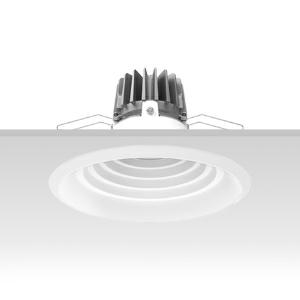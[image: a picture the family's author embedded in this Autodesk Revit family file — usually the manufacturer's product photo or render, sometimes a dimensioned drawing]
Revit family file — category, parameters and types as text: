
# Revit family: 3f_filippi_-_3f_reno_bianco_ugr_3f_filippi_-_30737_-_3f_reno_200_wh_2000-840_ep_ugr
name_source: partatom
category: Lighting Fixtures
units: mm (PartAtom-declared; Revit-internal decimal feet)

## family parameters
Cut with Voids When Loaded = No
Host = Face
Light Source = No
Part Type = Normal
Room Calculation Point = No
Round Connector Dimension = Use Diameter
Shared = No

## types (1)
- 3F Filippi - 3F Reno Bianco UGR (1 x LED, 2458 lm, 21 W, 4000 K)
    Apparent Load = 21 VA
    Approval mark = ENEC
    CIE Flux Codes = 90 100 100 100 100
    Color Rendering = 80
    Color Temperature = 4000 K
    Control Gear = Electronic ballast
    Default Elevation = 1800 mm
    Description = ILLUMINOTECHNICAL
Luminous efficiency 100% (DLOR 100%, ULOR 0%).
Initial luminous flux of the luminaire 2458 lm.
Emergency luminaire luminous flux BLF 20%.
Direct symmetric UGR distribution.
Installation Interdistance Transv.D = 0.99 x hu - Long.D = 1.01 x hu.
Average luminance <500 cd/m² for radial angles >65°.
Tabular UGR (CIE 117 - 4H-8H; S=0.25H; 70/50/20): RUG 17.4 - 17.3.
Beam angle: 64° - 65°.
Luminous efficacy 117 lm/W.
Lifetime (L90/B10): 30000 h. (tq+25°C)
Lifetime (L85/B10): 50000 h. (tq+25°C)
Lifetime (L70/B10): 80000 h. (tq+25°C)
Sudden decreased luminous flux after 50000 hours: 0% (C0).
Photobiological safety in compliance with IEC/TR 62778: RG0 risk exempt, (IEC 62471).
In compliance with IEC/EN 62722-2-1 - IEC/EN 62717 standards.

SOURCE
Compact LED module 2000/840.
Energy efficiency class (UE 2019/2020 - UE 2019/2015): D.
CIE 13.3 Colour rendering index: CRI >80 (R9 <50%).
IES TM-30 Fidelity Index: Rf = 84 Rg = 95.
CCT nominal colour temperature 4000 K.
Colour initial tolerance (MacAdam): SDCM 3.
Zhaga Book 3 compliant.

MECHANICAL
Passive heat dissipator in die-casting aluminium, oversized, for optimum thermal management of the LED module.
Parabolic element with graduated/concentric rings in white polycarbonate.
Internal specular metallic louvre to optimise control of the luminous flux in polycarbonate.
Transparent external lens with glossy and satin differentiated surfaces, with a cooling and anti-insect system in methacrylate (PMMA).
Fastening spring clips in stainless steel.
Dimensions: diameter 216 mm, height 142 mm. Weight 1.74 kg.
IP44 protection degree for exposed part, IP20 for recessed part.
Mechanical strength to impacts IK04 (0.5 joule).
Glow-wire test resistance 650°C.

ELECTRICAL
Wiring on a separate unit.
Halogen Free electronic wiring 230V-50/60Hz, power factor 0.90, THD <25%, constant output current, SELV, class II, 1 driver.
Power of the luminaire 21 W.
CE - IEC 60598-1 - EN 60598-1.
EP maintained emergency wiring on board, 1h duration, 24h recharge; compliant with EN 60598-2-22, excluding high risk areas.
SAFE FLICKER: PstLM=<1 and SVM=<0.4 (IEC TR 61547-1 and IEC TR 63158), to ensure a more comfortable and safe light.
Ambient temperature from +5°C to +25°C.
Temperature class T6 max 85°C.
Relative humidity UR: <85%.

INSTALLATION
Pull-up recessed fitting.
False ceiling carving: 200 mm.
All accessories dedicated to this product are available on the Catalog and on our website www.3F-Filippi.com.

APPLICATIONS
In environments with VDTs, managerial offices and staterooms, public offices and schools.
In false ceilings with narrow voids.

WARNING
Luminaire designed for disposal/recycling at end-of-life.
Replaceable (LED only) light source by a professional. Replaceable control gear by a professional.
    Height = 0 mm  [stored 0 ft]
    Lamp = 1 x LED
    Lamp Light Flux = 2458 lm
    Lamp Power = 21 W
    Lamp count = 1
    Length = 216 mm
    Lifetime = 50000 h
    Luminous efficacy = 117 lm/W
    Manufacturer = 3F Filippi
    ModVariant = No
    Model = 3F Filippi - 30737 - 3F Reno 200 WH 2000-840 EP UGR
    Mounting Place = Ceiling
    Mounting Type = Recessed
    Number of Poles = 1
    OnlyDefault = Yes
    Power Factor = 1
    Product Name = 3F Filippi - 3F Reno Bianco UGR
    Product group = recessed luminaire
    ProductGroupID = 4
    Protection Class = Protection class II
    Protection Degree = IP 20
    RLX_Detail_Level = 1
    RLX_Emergency_Light_Flux = 0 lm
    RLX_Emergency_Type = 0
    RLX_Emergency_Type_DB = No
    RlxData = <blob elided: 87129 chars, md5=3ff4f7c1>
    Socket = socket
    Standby Power = 0 W
    System Light Flux = 2458 lm
    System Power = 21 W
    Type Comments = Product without accessories
    Type Image = 3ffilippi_3f_reno_200_wh_2000.jpg
    URL = http://relux.com
    VarID = ---
    Voltage = 0 V
    Weight = 0.00 kg
    Width = 0 mm  [stored 0 ft]

note: [stored X ft] marks values corroborated as IEEE doubles in the binary element streams (Revit-internal decimal feet)

## geometry (parser evidence)
native form markers: Blend x4, Sweep x12
no freeform markers — native parametric forms only
